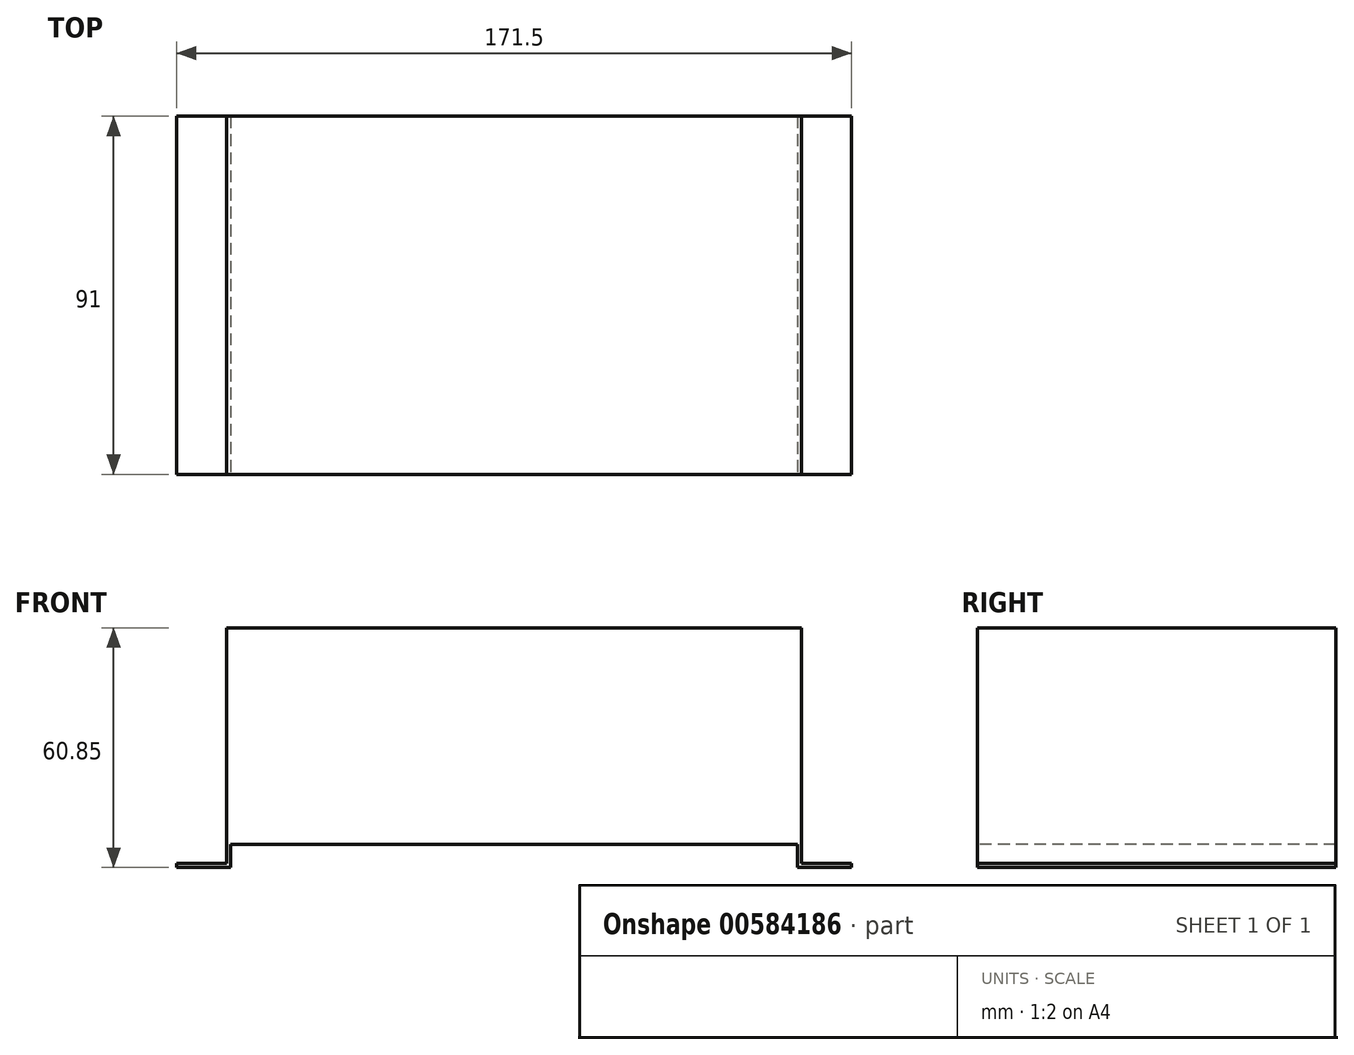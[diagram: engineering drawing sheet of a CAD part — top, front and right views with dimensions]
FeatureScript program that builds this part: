
annotation { "Feature Type Name" : "Feature", "Feature Type Description" : "" }
export const myFeature = defineFeature(function(context is Context, id is Id, definition is map)
    precondition{}
    {
        {
            var Q0;
            Q0=qCreatedBy(makeId("Top.planeOp"),FACE);
            var sketch = newSketch(context, id + "F0", { "sketchPlane" : qUnion([Q0])});
            skLineSegment(sketch, "E0.bottom", {"start": v(73, -45.5) * mm, "end": v(-73, -45.5) * mm});
            skLineSegment(sketch, "E0.top", {"start": v(73, 45.5) * mm, "end": v(-73, 45.5) * mm});
            skLineSegment(sketch, "E0.left", {"start": v(73, -45.5) * mm, "end": v(73, 45.5) * mm});
            skLineSegment(sketch, "E0.right", {"start": v(-73, -45.5) * mm, "end": v(-73, 45.5) * mm});
            skPoint(sketch, "E0.middle", {"position": v(0, 0) * mm});
            skSolve(sketch);
        }
        {
            var Q0;
            Q0 = qSketchRegion(id + "F0", true);
            extrude(context, id + "F1", {"entities" : qUnion([Q0]), "depth" : 55 * mm, "offsetDistance" : 25.4 * mm});
        }
        {
            var Q0;
            Q0=makeQuery(id+"F1.opExtrude","SWEPT_FACE",FACE,{"disambiguationData":[OSD([sQuery(id+"F0.wireOp",EDGE,"E0.bottom")])]});
            var sketch = newSketch(context, id + "F2", { "sketchPlane" : qUnion([Q0])});
            skLineSegment(sketch, "E1.bottom", {"start": v(-73, 0) * mm, "end": v(-72, 0) * mm});
            skLineSegment(sketch, "E1.top", {"start": v(-73, -5.85) * mm, "end": v(-72, -5.85) * mm});
            skLineSegment(sketch, "E1.left", {"start": v(-73, 0) * mm, "end": v(-73, -4.85) * mm});
            skLineSegment(sketch, "E1.right", {"start": v(-72, 0) * mm, "end": v(-72, -5.85) * mm});
            skLineSegment(sketch, "E2.bottom", {"start": v(-73, -5.85) * mm, "end": v(-85.75, -5.85) * mm});
            skLineSegment(sketch, "E2.top", {"start": v(-73, -4.85) * mm, "end": v(-85.75, -4.85) * mm});
            skLineSegment(sketch, "E2.right", {"start": v(-85.75, -5.85) * mm, "end": v(-85.75, -4.85) * mm});
            skLineSegment(sketch, "E3.bottom", {"start": v(73, 0) * mm, "end": v(72, 0) * mm});
            skLineSegment(sketch, "E3.top", {"start": v(73, -5.85) * mm, "end": v(72, -5.85) * mm});
            skLineSegment(sketch, "E3.left", {"start": v(73, 0) * mm, "end": v(73, -4.85) * mm});
            skLineSegment(sketch, "E3.right", {"start": v(72, 0) * mm, "end": v(72, -5.85) * mm});
            skLineSegment(sketch, "E4.bottom", {"start": v(73, -5.85) * mm, "end": v(85.75, -5.85) * mm});
            skLineSegment(sketch, "E4.top", {"start": v(73, -4.85) * mm, "end": v(85.75, -4.85) * mm});
            skLineSegment(sketch, "E4.right", {"start": v(85.75, -5.85) * mm, "end": v(85.75, -4.85) * mm});
            skSolve(sketch);
        }
        {
            var Q0;
            Q0 = qSketchRegion(id + "F2", true);
            var Q1;
            Q1=makeQuery(id+"F1.opExtrude","SWEPT_FACE",FACE,{"disambiguationData":[OSD([sQuery(id+"F0.wireOp",EDGE,"E0.top")])]});
            extrude(context, id + "F3", {"entities" : qUnion([Q0]), "operationType" : NewBodyOperationType.ADD, "endBound" : BoundingType.UP_TO_SURFACE, "oppositeDirection" : true, "depth" : 25.4 * mm, "endBoundEntityFace" : qUnion([Q1]), "offsetDistance" : 25.4 * mm});
        }
    });
